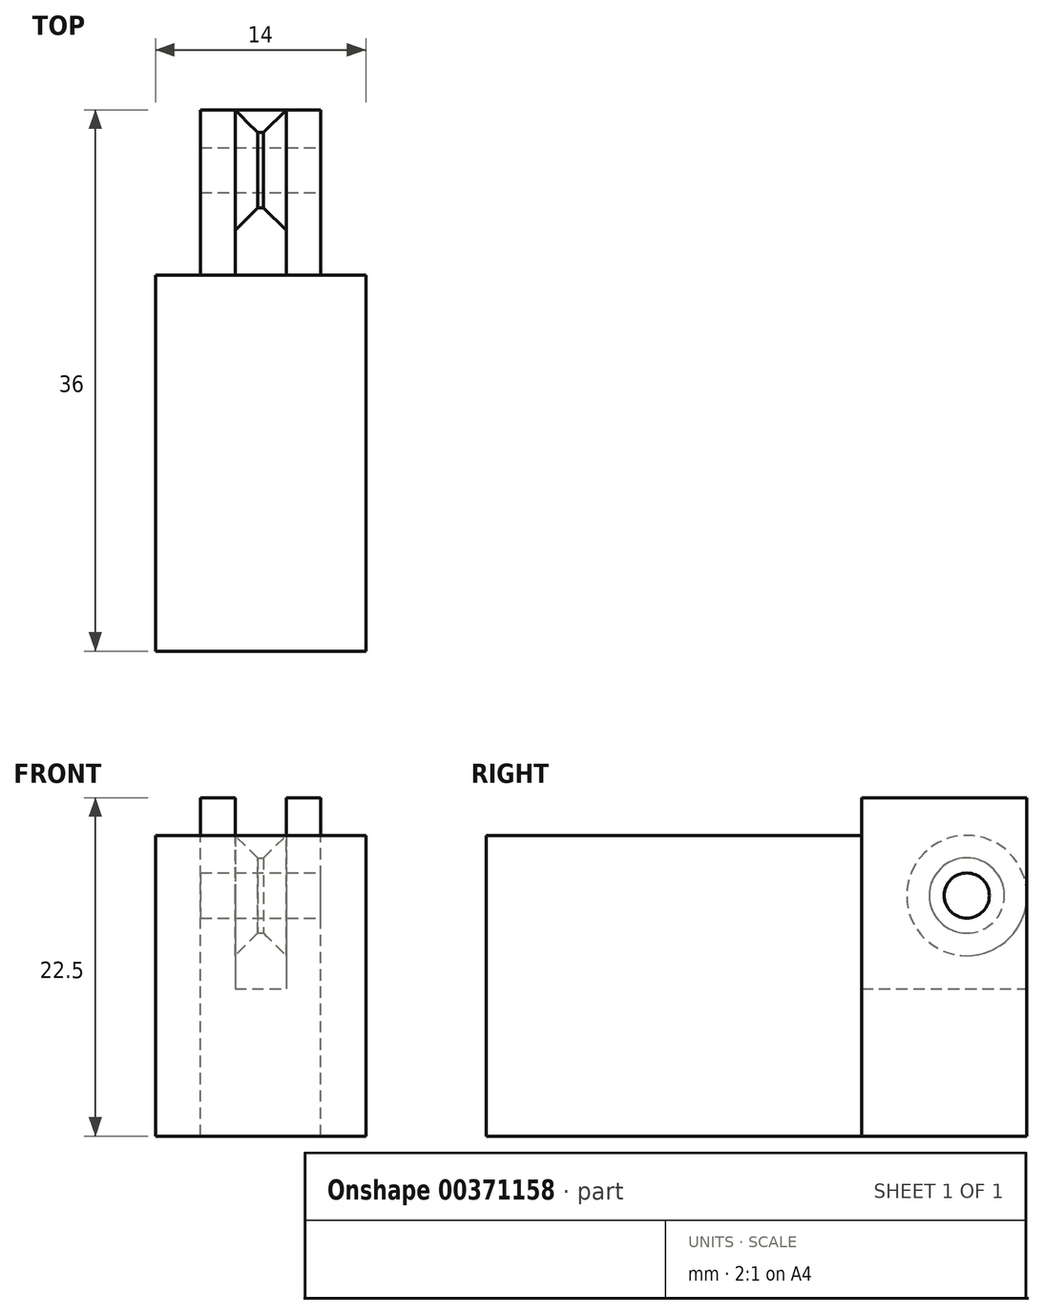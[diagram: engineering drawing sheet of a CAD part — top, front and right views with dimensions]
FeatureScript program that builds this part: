
annotation { "Feature Type Name" : "Feature", "Feature Type Description" : "" }
export const myFeature = defineFeature(function(context is Context, id is Id, definition is map)
    precondition{}
    {
        {
            var Q0;
            Q0=qCreatedBy(makeId("Front.planeOp"),FACE);
            var sketch = newSketch(context, id + "F0", { "sketchPlane" : qUnion([Q0])});
            skLineSegment(sketch, "E0", {"start": v(0, 0) * mm, "end": v(-4, 0) * mm});
            skLineSegment(sketch, "E1", {"start": v(-4, 0) * mm, "end": v(-4, 22.5) * mm});
            skLineSegment(sketch, "E2", {"start": v(-4, 22.5) * mm, "end": v(-1.7, 22.5) * mm});
            skLineSegment(sketch, "E3", {"start": v(-1.7, 22.5) * mm, "end": v(-1.7, 0) * mm, "construction": true});
            skPoint(sketch, "E3.endSnap0", {"position": v(-2, 0) * mm});
            skLineSegment(sketch, "E4", {"start": v(-1.7, 0) * mm, "end": v(-1.7, 9.8) * mm, "construction": true});
            skLineSegment(sketch, "E5", {"start": v(-1.7, 22.5) * mm, "end": v(-1.7, 9.8) * mm});
            skLineSegment(sketch, "E6", {"start": v(-1.7, 9.8) * mm, "end": v(0, 9.8) * mm});
            skLineSegment(sketch, "E7", {"start": v(0, 9.8) * mm, "end": v(0, 0) * mm});
            skSolve(sketch);
        }
        {
            var Q0;
            Q0=makeQuery(id+"F0.imprint","IMPRINT",FACE,{"disambiguationData":[TD([[makeQuery(id+"F0.imprint","IMPRINT",EDGE,{"derivedFrom":sQuery(id+"F0.wireOp",EDGE,"E0")}),-1.0]])]});
            extrude(context, id + "F1", {"entities" : qUnion([Q0]), "depth" : 11 * mm});
        }
        {
            var Q0;
            Q0=makeQuery(id+"F1.opExtrude","SWEPT_BODY",BODY,{"disambiguationData":[OSD([sQuery(id+"F0.wireOp",EDGE,"E0"),sQuery(id+"F0.wireOp",EDGE,"E1"),sQuery(id+"F0.wireOp",EDGE,"E2"),sQuery(id+"F0.wireOp",EDGE,"E5"),sQuery(id+"F0.wireOp",EDGE,"E6"),sQuery(id+"F0.wireOp",EDGE,"E7")])]});
            var Q1;
            Q1=makeQuery(id+"F1.opExtrude","SWEPT_FACE",FACE,{"disambiguationData":[OSD([sQuery(id+"F0.wireOp",EDGE,"E7")])]});
            mirror(context, id + "F2", {"operationType" : NewBodyOperationType.ADD, "entities" : qUnion([Q0]), "mirrorPlane" : qUnion([Q1])});
        }
        {
            var Q0;
            {var subQ0=makeQuery(id+"F1.opExtrude","CAP_FACE",FACE,{"disambiguationData":[OSD([sQuery(id+"F0.wireOp",EDGE,"E0"),sQuery(id+"F0.wireOp",EDGE,"E1"),sQuery(id+"F0.wireOp",EDGE,"E2"),sQuery(id+"F0.wireOp",EDGE,"E5"),sQuery(id+"F0.wireOp",EDGE,"E6"),sQuery(id+"F0.wireOp",EDGE,"E7")])],"isStart":false});Q0=makeQuery(id+"F2.boolean.opBoolean","MERGE",FACE,{"derivedFrom":[subQ0,makeQuery(id+"F2.opPattern","COPY",FACE,{"derivedFrom":subQ0,"instanceName":"1"})]});}
            var sketch = newSketch(context, id + "F3", { "sketchPlane" : qUnion([Q0])});
            skLineSegment(sketch, "E8", {"start": v(0, 0) * mm, "end": v(-7, 0) * mm, "construction": true});
            skLineSegment(sketch, "E9", {"start": v(0, 0) * mm, "end": v(-7, 0) * mm});
            skLineSegment(sketch, "E10", {"start": v(-7, 0) * mm, "end": v(-7, 20) * mm});
            skLineSegment(sketch, "E11", {"start": v(0, 0) * mm, "end": v(7, 0) * mm});
            skLineSegment(sketch, "E12", {"start": v(7, 0) * mm, "end": v(7, 20) * mm});
            skLineSegment(sketch, "E13", {"start": v(-7, 20) * mm, "end": v(7, 20) * mm});
            skSolve(sketch);
        }
        {
            var Q0;
            {var subQ3=sQuery(id+"F3.wireOp",EDGE,"E12");Q0=makeQuery(id+"F3.imprint","IMPRINT",FACE,{"disambiguationData":[TD([[makeQuery(id+"F3.imprint","IMPRINT",EDGE,{"derivedFrom":subQ3}),1.0]])]});}
            var Q1;
            {var subQ13=makeQuery(id+"F1.opExtrude","CAP_EDGE",EDGE,{"disambiguationData":[OSD([sQuery(id+"F0.wireOp",EDGE,"E6")])],"isStart":false});var subQ14=makeQuery(id+"F2.boolean.opBoolean","MERGE",EDGE,{"derivedFrom":[subQ13,makeQuery(id+"F2.opPattern","COPY",EDGE,{"derivedFrom":subQ13,"instanceName":"1"})]});Q1=makeQuery(id+"F3.imprint","IMPRINT",FACE,{"disambiguationData":[TD([[makeQuery(id+"F3.imprint","IMPRINT",EDGE,{"derivedFrom":subQ14}),-1.0]])]});}
            var Q2;
            {var subQ5=makeQuery(id+"F1.opExtrude","CAP_EDGE",EDGE,{"disambiguationData":[OSD([sQuery(id+"F0.wireOp",EDGE,"E6")])],"isStart":false});var subQ6=makeQuery(id+"F2.boolean.opBoolean","MERGE",EDGE,{"derivedFrom":[subQ5,makeQuery(id+"F2.opPattern","COPY",EDGE,{"derivedFrom":subQ5,"instanceName":"1"})]});Q2=makeQuery(id+"F3.imprint","IMPRINT",FACE,{"disambiguationData":[TD([[makeQuery(id+"F3.imprint","IMPRINT",EDGE,{"derivedFrom":subQ6}),1.0]])]});}
            var Q3;
            {var subQ3=sQuery(id+"F3.wireOp",EDGE,"E10");Q3=makeQuery(id+"F3.imprint","IMPRINT",FACE,{"disambiguationData":[TD([[makeQuery(id+"F3.imprint","IMPRINT",EDGE,{"derivedFrom":subQ3}),-1.0]])]});}
            extrude(context, id + "F4", {"entities" : qUnion([Q0, Q1, Q2, Q3]), "operationType" : NewBodyOperationType.ADD, "depth" : 25 * mm});
        }
        {
            var Q0;
            Q0=makeQuery(id+"F2.opPattern","COPY",FACE,{"derivedFrom":makeQuery(id+"F1.opExtrude","SWEPT_FACE",FACE,{"disambiguationData":[OSD([sQuery(id+"F0.wireOp",EDGE,"E1")])]}),"instanceName":"1"});
            var sketch = newSketch(context, id + "F5", { "sketchPlane" : qUnion([Q0])});
            skLineSegment(sketch, "E14", {"start": v(0, 16) * mm, "end": v(-4, 16) * mm, "construction": true});
            skLineSegment(sketch, "E15", {"start": v(-4, 16) * mm, "end": v(-4, 0) * mm, "construction": true});
            skCircle(sketch, "E16", {"center": v(-4, 16) * mm, "radius": 1.5 * mm});
            skCircle(sketch, "E17", {"center": v(-4, 16) * mm, "radius": 2.5 * mm});
            skSolve(sketch);
        }
        {
            var Q0;
            Q0=makeQuery(id+"F5.imprint","IMPRINT",FACE,{"disambiguationData":[TD([[makeQuery(id+"F5.imprint","IMPRINT",EDGE,{"derivedFrom":sQuery(id+"F5.wireOp",EDGE,"E16")}),1.0]])]});
            extrude(context, id + "F6", {"entities" : qUnion([Q0]), "operationType" : NewBodyOperationType.REMOVE, "oppositeDirection" : true, "depth" : 25 * mm});
        }
        {
            var Q0;
            Q0=makeQuery(id+"F5.imprint","IMPRINT",FACE,{"disambiguationData":[TD([[makeQuery(id+"F5.imprint","IMPRINT",EDGE,{"derivedFrom":sQuery(id+"F5.wireOp",EDGE,"E16")}),-1.0]])]});
            var Q1;
            Q1=makeQuery(id+"F1.opExtrude","SWEPT_FACE",FACE,{"disambiguationData":[OSD([sQuery(id+"F0.wireOp",EDGE,"E1")])]});
            extrude(context, id + "F7", {"entities" : qUnion([Q0]), "operationType" : NewBodyOperationType.ADD, "endBound" : BoundingType.UP_TO_SURFACE, "oppositeDirection" : true, "endBoundEntityFace" : qUnion([Q1]), "depth" : 25 * mm});
        }
        {
            var Q0;
            Q0=makeQuery(id+"F7.boolean.opBoolean","INTERSECT",EDGE,{"derivedFrom":[makeQuery(id+"F1.opExtrude","SWEPT_FACE",FACE,{"disambiguationData":[OSD([sQuery(id+"F0.wireOp",EDGE,"E5")])]}),makeQuery(id+"F7.opExtrude","SWEPT_FACE",FACE,{"disambiguationData":[OSD([sQuery(id+"F5.wireOp",EDGE,"E17")])]})]});
            chamfer(context, id + "F8", {"entities" : qUnion([Q0]), "width" : 1.5 * mm, "tangentPropagation" : true});
        }
        {
            var Q0;
            Q0=makeQuery(id+"F7.boolean.opBoolean","INTERSECT",EDGE,{"derivedFrom":[makeQuery(id+"F2.opPattern","COPY",FACE,{"derivedFrom":makeQuery(id+"F1.opExtrude","SWEPT_FACE",FACE,{"disambiguationData":[OSD([sQuery(id+"F0.wireOp",EDGE,"E5")])]}),"instanceName":"1"}),makeQuery(id+"F7.opExtrude","SWEPT_FACE",FACE,{"disambiguationData":[OSD([sQuery(id+"F5.wireOp",EDGE,"E17")])]})]});
            chamfer(context, id + "F9", {"entities" : qUnion([Q0]), "width" : 1.5 * mm, "tangentPropagation" : true});
        }
    });
